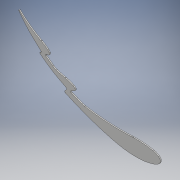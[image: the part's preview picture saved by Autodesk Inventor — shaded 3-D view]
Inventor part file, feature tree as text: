
AUTODESK INVENTOR PART (.ipt)
format: ipt  version: 2018.2 (Build 222227000, 227)  size: 183,808 bytes
history: native  units: mm
features: projected_geometry x3, extrude x1, fillet x1, sketch x1
ambient origin geometry x8: Origin, YZ Plane, XZ Plane, XY Plane, X Axis, Y Axis, Z Axis, Center Point
bodies: Body1 (feature_tree)
feature tree (6):
  extrude  "押し出し1"  TaperAngle=45.0deg  [1 undecoded]
  fillet  "フィレット1"  [1 undecoded]
  sketch  "スケッチ1"
  projected_geometry  "投影ループ1"
  projected_geometry  "投影ループ2"
  projected_geometry  "投影ループ3"
note: 2 required parameter values undecoded (feature->parameter linkage not recoverable at this tier; creation-order binding heuristic only, values carry confidence <= 0.55)
